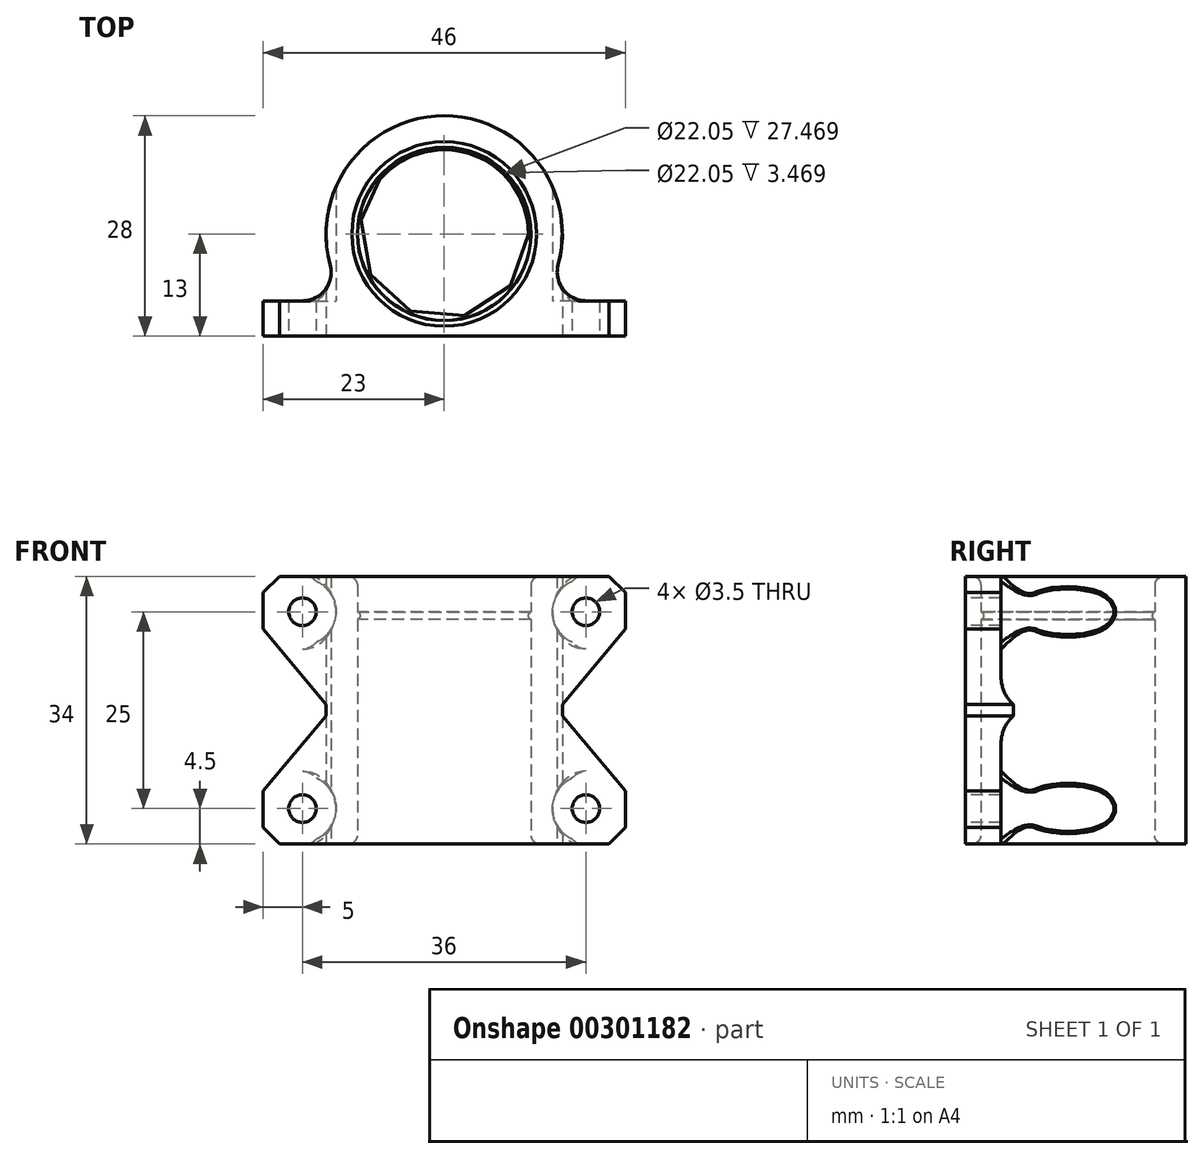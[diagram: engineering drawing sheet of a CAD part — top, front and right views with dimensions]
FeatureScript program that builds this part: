
annotation { "Feature Type Name" : "Feature", "Feature Type Description" : "" }
export const myFeature = defineFeature(function(context is Context, id is Id, definition is map)
    precondition{}
    {
        {
            var Q0;
            Q0=qCreatedBy(makeId("Top.planeOp"),FACE);
            var sketch = newSketch(context, id + "F0", { "sketchPlane" : qUnion([Q0])});
            skLineSegment(sketch, "E0.bottom", {"start": v(-23, 0) * mm, "end": v(23, 0) * mm});
            skLineSegment(sketch, "E0.left", {"start": v(-23, 0) * mm, "end": v(-23, 4.5) * mm});
            skLineSegment(sketch, "E0.right", {"start": v(23, 0) * mm, "end": v(23, 4.5) * mm});
            skCircle(sketch, "E1", {"center": v(0, 13) * mm, "radius": 11.03 * mm});
            skArc(sketch, "E2", {"start": v(-14.48, 9.1) * mm, "mid": v(0, -2) * mm, "end": v(14.48, 9.1) * mm, "construction": true});
            skArc(sketch, "E3", {"start": v(14.48, 9.1) * mm, "mid": v(0, 28) * mm, "end": v(-14.48, 9.1) * mm});
            skLineSegment(sketch, "E4", {"start": v(23, 4.5) * mm, "end": v(18, 4.5) * mm});
            skLineSegment(sketch, "E5", {"start": v(-23, 4.5) * mm, "end": v(-18, 4.5) * mm});
            skArc(sketch, "E6", {"start": v(18, 4.5) * mm, "mid": v(15.1, 5.93) * mm, "end": v(14.48, 9.1) * mm});
            skArc(sketch, "E7", {"start": v(-18, 4.5) * mm, "mid": v(-15.1, 5.93) * mm, "end": v(-14.48, 9.1) * mm});
            skSolve(sketch);
        }
        {
            var Q0;
            Q0=makeQuery(id+"F0.imprint","IMPRINT",FACE,{"disambiguationData":[TD([[makeQuery(id+"F0.imprint","IMPRINT",EDGE,{"derivedFrom":sQuery(id+"F0.wireOp",EDGE,"E0.bottom")}),1.0]])]});
            extrude(context, id + "F1", {"entities" : qUnion([Q0]), "endBound" : BoundingType.SYMMETRIC, "depth" : 34 * mm});
        }
        {
            var Q0;
            Q0=makeQuery(id+"F1.opExtrude","SWEPT_FACE",FACE,{"disambiguationData":[OSD([sQuery(id+"F0.wireOp",EDGE,"E0.bottom")])]});
            var sketch = newSketch(context, id + "F2", { "sketchPlane" : qUnion([Q0])});
            skLineSegment(sketch, "E8.bottom", {"start": v(18, 12.5) * mm, "end": v(-18, 12.5) * mm, "construction": true});
            skLineSegment(sketch, "E8.top", {"start": v(18, -12.5) * mm, "end": v(-18, -12.5) * mm, "construction": true});
            skLineSegment(sketch, "E8.left", {"start": v(18, 12.5) * mm, "end": v(18, -12.5) * mm, "construction": true});
            skLineSegment(sketch, "E8.right", {"start": v(-18, 12.5) * mm, "end": v(-18, -12.5) * mm, "construction": true});
            skPoint(sketch, "E8.middle", {"position": v(0, 0) * mm});
            skCircle(sketch, "E9", {"center": v(-18, 12.5) * mm, "radius": 1.75 * mm});
            skCircle(sketch, "E10", {"center": v(18, 12.5) * mm, "radius": 1.75 * mm});
            skCircle(sketch, "E11", {"center": v(18, -12.5) * mm, "radius": 1.75 * mm});
            skCircle(sketch, "E12", {"center": v(-18, -12.5) * mm, "radius": 1.75 * mm});
            skCircle(sketch, "E13", {"center": v(-18, 12.5) * mm, "radius": 4.25 * mm});
            skCircle(sketch, "E14", {"center": v(18, 12.5) * mm, "radius": 4.25 * mm});
            skCircle(sketch, "E15", {"center": v(-18, -12.5) * mm, "radius": 4.25 * mm});
            skCircle(sketch, "E16", {"center": v(18, -12.5) * mm, "radius": 4.25 * mm});
            skLineSegment(sketch, "E17.0", {"start": v(-23, 17) * mm, "end": v(-23, -17) * mm});
            skLineSegment(sketch, "E17.1", {"start": v(23, 17) * mm, "end": v(23, -17) * mm});
            skPoint(sketch, "E18.0", {"position": v(-15, 0) * mm});
            skPoint(sketch, "E18.1", {"position": v(15, 0) * mm});
            skLineSegment(sketch, "E19", {"start": v(-23, -14.92) * mm, "end": v(-20.92, -17) * mm});
            skLineSegment(sketch, "E20", {"start": v(-23, 14.92) * mm, "end": v(-20.92, 17) * mm});
            skLineSegment(sketch, "E21", {"start": v(23, 14.92) * mm, "end": v(20.92, 17) * mm});
            skLineSegment(sketch, "E22", {"start": v(23, -14.92) * mm, "end": v(20.92, -17) * mm});
            skLineSegment(sketch, "E23", {"start": v(-15, 0.76) * mm, "end": v(-15, -0.76) * mm});
            skLineSegment(sketch, "E24", {"start": v(-23, 10.3) * mm, "end": v(-15, 0.76) * mm});
            skLineSegment(sketch, "E25", {"start": v(-15, -0.76) * mm, "end": v(-23, -10.3) * mm});
            skLineSegment(sketch, "E26", {"start": v(15, 0.76) * mm, "end": v(15, -0.76) * mm});
            skLineSegment(sketch, "E27", {"start": v(15, 0.76) * mm, "end": v(23, 10.3) * mm});
            skLineSegment(sketch, "E28", {"start": v(15, -0.76) * mm, "end": v(23, -10.3) * mm});
            skLineSegment(sketch, "E29.0", {"start": v(-15, 0) * mm, "end": v(15, 0) * mm});
            skSolve(sketch);
        }
        {
            var Q0;
            Q0=makeQuery(id+"F2.imprint","IMPRINT",FACE,{"disambiguationData":[TD([[makeQuery(id+"F2.imprint","IMPRINT",EDGE,{"derivedFrom":sQuery(id+"F2.wireOp",EDGE,"E23")}),-1.0]])]});
            var Q1;
            {var subQ3=sQuery(id+"F2.wireOp",EDGE,"E20");Q1=makeQuery(id+"F2.imprint","IMPRINT",FACE,{"disambiguationData":[TD([[makeQuery(id+"F2.imprint","IMPRINT",EDGE,{"derivedFrom":subQ3}),1.0]])]});}
            var Q2;
            Q2=makeQuery(id+"F2.imprint","IMPRINT",FACE,{"disambiguationData":[TD([[makeQuery(id+"F2.imprint","IMPRINT",EDGE,{"derivedFrom":sQuery(id+"F2.wireOp",EDGE,"E9")}),1.0]])]});
            var Q3;
            Q3=makeQuery(id+"F2.imprint","IMPRINT",FACE,{"disambiguationData":[TD([[makeQuery(id+"F2.imprint","IMPRINT",EDGE,{"derivedFrom":sQuery(id+"F2.wireOp",EDGE,"E10")}),1.0]])]});
            var Q4;
            Q4=makeQuery(id+"F2.imprint","IMPRINT",FACE,{"disambiguationData":[TD([[makeQuery(id+"F2.imprint","IMPRINT",EDGE,{"derivedFrom":sQuery(id+"F2.wireOp",EDGE,"E11")}),1.0]])]});
            var Q5;
            Q5=makeQuery(id+"F2.imprint","IMPRINT",FACE,{"disambiguationData":[TD([[makeQuery(id+"F2.imprint","IMPRINT",EDGE,{"derivedFrom":sQuery(id+"F2.wireOp",EDGE,"E12")}),1.0]])]});
            var Q6;
            {var subQ3=sQuery(id+"F2.wireOp",EDGE,"E19");Q6=makeQuery(id+"F2.imprint","IMPRINT",FACE,{"disambiguationData":[TD([[makeQuery(id+"F2.imprint","IMPRINT",EDGE,{"derivedFrom":subQ3}),-1.0]])]});}
            var Q7;
            {var subQ3=sQuery(id+"F2.wireOp",EDGE,"E22");Q7=makeQuery(id+"F2.imprint","IMPRINT",FACE,{"disambiguationData":[TD([[makeQuery(id+"F2.imprint","IMPRINT",EDGE,{"derivedFrom":subQ3}),1.0]])]});}
            var Q8;
            Q8=makeQuery(id+"F2.imprint","IMPRINT",FACE,{"disambiguationData":[TD([[makeQuery(id+"F2.imprint","IMPRINT",EDGE,{"derivedFrom":sQuery(id+"F2.wireOp",EDGE,"E26")}),1.0]])]});
            var Q9;
            {var subQ3=sQuery(id+"F2.wireOp",EDGE,"E21");Q9=makeQuery(id+"F2.imprint","IMPRINT",FACE,{"disambiguationData":[TD([[makeQuery(id+"F2.imprint","IMPRINT",EDGE,{"derivedFrom":subQ3}),-1.0]])]});}
            extrude(context, id + "F3", {"entities" : qUnion([Q0, Q1, Q2, Q3, Q4, Q5, Q6, Q7, Q8, Q9]), "operationType" : NewBodyOperationType.REMOVE, "endBound" : BoundingType.THROUGH_ALL, "oppositeDirection" : true, "depth" : 25 * mm});
        }
        {
            var Q0;
            {var subQ2=sQuery(id+"F0.wireOp",EDGE,"E4");Q0=makeQuery(id+"F3.boolean.opBoolean","SPLIT",FACE,{"disambiguationData":[TD([makeQuery(id+"F3.opExtrude","SWEPT_FACE",FACE,{"disambiguationData":[OSD([sQuery(id+"F2.wireOp",EDGE,"E10")])]})])],"derivedFrom":makeQuery(id+"F1.opExtrude","SWEPT_FACE",FACE,{"disambiguationData":[OSD([subQ2])]})});}
            var sketch = newSketch(context, id + "F4", { "sketchPlane" : qUnion([Q0])});
            skCircle(sketch, "E30.0", {"center": v(-18, 12.5) * mm, "radius": 4.25 * mm});
            skCircle(sketch, "E30.1", {"center": v(-18, -12.5) * mm, "radius": 4.25 * mm});
            skCircle(sketch, "E30.2", {"center": v(18, 12.5) * mm, "radius": 4.25 * mm});
            skCircle(sketch, "E30.3", {"center": v(18, -12.5) * mm, "radius": 4.25 * mm});
            skSolve(sketch);
        }
        {
            var Q0;
            Q0 = qSketchRegion(id + "F4", true);
            extrude(context, id + "F5", {"entities" : qUnion([Q0]), "operationType" : NewBodyOperationType.REMOVE, "endBound" : BoundingType.THROUGH_ALL, "depth" : 25 * mm});
        }
        {
            var Q0;
            Q0=makeQuery(id+"F1.opExtrude","CAP_FACE",FACE,{"disambiguationData":[OSD([sQuery(id+"F0.wireOp",EDGE,"E0.bottom"),sQuery(id+"F0.wireOp",EDGE,"E0.left"),sQuery(id+"F0.wireOp",EDGE,"E0.right"),sQuery(id+"F0.wireOp",EDGE,"47fbd2f8-fe7f-4e0c-9e9a-158b01d105e2"),sQuery(id+"F0.wireOp",EDGE,"4dd4db88-c3c4-4c66-9c3d-1c3a97fc9206"),sQuery(id+"F0.wireOp",EDGE,"E1"),sQuery(id+"F0.wireOp",EDGE,"E3")])],"isStart":false});
            cPlane(context, id + "F6", {"entities" : qUnion([Q0]), "cplaneType" : CPlaneType.OFFSET, "offset" : 5.5 * mm, "oppositeDirection" : true, "width" : 150 * mm, "height" : 150 * mm});
        }
        {
            var Q0;
            Q0=qCreatedBy(id+"F6.planeOp",FACE);
            var sketch = newSketch(context, id + "F7", { "sketchPlane" : qUnion([Q0])});
            skCircle(sketch, "E31.0", {"center": v(0, 13) * mm, "radius": 11.03 * mm});
            skCircle(sketch, "E32", {"center": v(0, 13) * mm, "radius": 10.7 * mm});
            skSolve(sketch);
        }
        {
            var Q0;
            Q0=makeQuery(id+"F7.imprint","IMPRINT",FACE,{"disambiguationData":[TD([[makeQuery(id+"F7.imprint","IMPRINT",EDGE,{"derivedFrom":sQuery(id+"F7.wireOp",EDGE,"E31.0")}),1.0]])]});
            extrude(context, id + "F8", {"entities" : qUnion([Q0]), "operationType" : NewBodyOperationType.ADD, "depth" : 1 * mm});
        }
        {
            var Q0;
            Q0=makeQuery(id+"F8.opExtrude","CAP_EDGE",EDGE,{"disambiguationData":[OSD([sQuery(id+"F7.wireOp",EDGE,"E32")])],"isStart":false});
            var Q1;
            Q1=makeQuery(id+"F8.opExtrude","CAP_EDGE",EDGE,{"disambiguationData":[OSD([sQuery(id+"F7.wireOp",EDGE,"E32")])],"isStart":true});
            chamfer(context, id + "F9", {"entities" : qUnion([Q0, Q1]), "chamferType" : ChamferType.TWO_OFFSETS, "width1" : 0.3 * mm, "oppositeDirection" : false, "width2" : 0.3 * mm, "tangentPropagation" : true});
        }
        {
            var Q0;
            {var subQ0=sQuery(id+"F7.wireOp",EDGE,"E32");Q0=makeQuery(id+"F9.opChamfer","BLEND_EDGE",EDGE,{"blendedFrom":[makeQuery(id+"F8.opExtrude","CAP_EDGE",EDGE,{"disambiguationData":[OSD([subQ0])],"isStart":false}),makeQuery(id+"F8.opExtrude","SWEPT_FACE",FACE,{"disambiguationData":[OSD([subQ0])]})],"blendedInto":[makeQuery(id+"F8.opExtrude","SWEPT_FACE",FACE,{"disambiguationData":[OSD([subQ0])]})]});}
            var Q1;
            {var subQ0=sQuery(id+"F7.wireOp",EDGE,"E32");Q1=makeQuery(id+"F9.opChamfer","BLEND_EDGE",EDGE,{"blendedFrom":[makeQuery(id+"F8.opExtrude","CAP_EDGE",EDGE,{"disambiguationData":[OSD([subQ0])],"isStart":true}),makeQuery(id+"F8.opExtrude","SWEPT_FACE",FACE,{"disambiguationData":[OSD([subQ0])]})],"blendedInto":[makeQuery(id+"F8.opExtrude","SWEPT_FACE",FACE,{"disambiguationData":[OSD([subQ0])]})]});}
            fillet(context, id + "F10", {"entities" : qUnion([Q0, Q1]), "radius" : 0.48 * mm, "tangentPropagation" : true, "allowEdgeOverflow" : false});
        }
        {
            var Q0;
            Q0=makeQuery(id+"F1.opExtrude","CAP_EDGE",EDGE,{"disambiguationData":[OSD([sQuery(id+"F0.wireOp",EDGE,"E1")])],"isStart":false});
            var Q1;
            Q1=makeQuery(id+"F1.opExtrude","CAP_EDGE",EDGE,{"disambiguationData":[OSD([sQuery(id+"F0.wireOp",EDGE,"E1")])],"isStart":true});
            chamfer(context, id + "F11", {"entities" : qUnion([Q0, Q1]), "width" : 0.7 * mm, "tangentPropagation" : true});
        }
        {
            var Q0;
            {var subQ0=sQuery(id+"F0.wireOp",EDGE,"E1");Q0=makeQuery(id+"F11.opChamfer","BLEND_EDGE",EDGE,{"blendedFrom":[makeQuery(id+"F1.opExtrude","CAP_EDGE",EDGE,{"disambiguationData":[OSD([subQ0])],"isStart":true}),makeQuery(id+"F8.boolean.opBoolean","SPLIT",FACE,{"disambiguationData":[TD([makeQuery(id+"F8.opExtrude","CAP_FACE",FACE,{"disambiguationData":[OSD([sQuery(id+"F7.wireOp",EDGE,"E31.0"),sQuery(id+"F7.wireOp",EDGE,"E32")])],"isStart":true})])],"derivedFrom":makeQuery(id+"F1.opExtrude","SWEPT_FACE",FACE,{"disambiguationData":[OSD([subQ0])]})})],"blendedInto":[makeQuery(id+"F8.boolean.opBoolean","SPLIT",FACE,{"disambiguationData":[TD([makeQuery(id+"F8.opExtrude","CAP_FACE",FACE,{"disambiguationData":[OSD([sQuery(id+"F7.wireOp",EDGE,"E31.0"),sQuery(id+"F7.wireOp",EDGE,"E32")])],"isStart":true})])],"derivedFrom":makeQuery(id+"F1.opExtrude","SWEPT_FACE",FACE,{"disambiguationData":[OSD([subQ0])]})})]});}
            var Q1;
            {var subQ0=sQuery(id+"F0.wireOp",EDGE,"E1");Q1=makeQuery(id+"F11.opChamfer","BLEND_EDGE",EDGE,{"blendedFrom":[makeQuery(id+"F1.opExtrude","CAP_EDGE",EDGE,{"disambiguationData":[OSD([subQ0])],"isStart":false}),makeQuery(id+"F8.boolean.opBoolean","SPLIT",FACE,{"disambiguationData":[TD([makeQuery(id+"F8.opExtrude","CAP_FACE",FACE,{"disambiguationData":[OSD([sQuery(id+"F7.wireOp",EDGE,"E31.0"),sQuery(id+"F7.wireOp",EDGE,"E32")])],"isStart":false})])],"derivedFrom":makeQuery(id+"F1.opExtrude","SWEPT_FACE",FACE,{"disambiguationData":[OSD([subQ0])]})})],"blendedInto":[makeQuery(id+"F8.boolean.opBoolean","SPLIT",FACE,{"disambiguationData":[TD([makeQuery(id+"F8.opExtrude","CAP_FACE",FACE,{"disambiguationData":[OSD([sQuery(id+"F7.wireOp",EDGE,"E31.0"),sQuery(id+"F7.wireOp",EDGE,"E32")])],"isStart":false})])],"derivedFrom":makeQuery(id+"F1.opExtrude","SWEPT_FACE",FACE,{"disambiguationData":[OSD([subQ0])]})})]});}
            fillet(context, id + "F12", {"entities" : qUnion([Q0, Q1]), "radius" : 0.8 * mm, "tangentPropagation" : true, "allowEdgeOverflow" : false});
        }
        {
            var Q0;
            Q0=makeQuery(id+"F5.boolean.opBoolean","INTERSECT",EDGE,{"disambiguationData":[OD(1.0)],"derivedFrom":[makeQuery(id+"F1.opExtrude","SWEPT_FACE",FACE,{"disambiguationData":[OSD([sQuery(id+"F0.wireOp",EDGE,"E7")])]}),makeQuery(id+"F5.opExtrude","SWEPT_FACE",FACE,{"disambiguationData":[OSD([sQuery(id+"F4.wireOp",EDGE,"E30.2")])]})]});
            var Q1;
            Q1=makeQuery(id+"F5.boolean.opBoolean","INTERSECT",EDGE,{"disambiguationData":[OD(1.0)],"derivedFrom":[makeQuery(id+"F1.opExtrude","SWEPT_FACE",FACE,{"disambiguationData":[OSD([sQuery(id+"F0.wireOp",EDGE,"E7")])]}),makeQuery(id+"F5.opExtrude","SWEPT_FACE",FACE,{"disambiguationData":[OSD([sQuery(id+"F4.wireOp",EDGE,"E30.3")])]})]});
            var Q2;
            Q2=makeQuery(id+"F5.boolean.opBoolean","INTERSECT",EDGE,{"disambiguationData":[OD(1.0)],"derivedFrom":[makeQuery(id+"F1.opExtrude","SWEPT_FACE",FACE,{"disambiguationData":[OSD([sQuery(id+"F0.wireOp",EDGE,"E6")])]}),makeQuery(id+"F5.opExtrude","SWEPT_FACE",FACE,{"disambiguationData":[OSD([sQuery(id+"F4.wireOp",EDGE,"E30.1")])]})]});
            var Q3;
            Q3=makeQuery(id+"F5.boolean.opBoolean","INTERSECT",EDGE,{"disambiguationData":[OD(1.0)],"derivedFrom":[makeQuery(id+"F1.opExtrude","SWEPT_FACE",FACE,{"disambiguationData":[OSD([sQuery(id+"F0.wireOp",EDGE,"E6")])]}),makeQuery(id+"F5.opExtrude","SWEPT_FACE",FACE,{"disambiguationData":[OSD([sQuery(id+"F4.wireOp",EDGE,"E30.0")])]})]});
            chamfer(context, id + "F13", {"entities" : qUnion([Q0, Q1, Q2, Q3]), "width" : 0.5 * mm, "tangentPropagation" : true});
        }
    });
